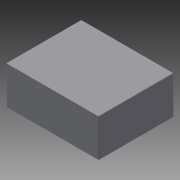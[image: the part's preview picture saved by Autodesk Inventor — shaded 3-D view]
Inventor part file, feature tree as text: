
AUTODESK INVENTOR PART (.ipt)
format: ipt  version: 2014 (Build 180170000, 170)  size: 89,088 bytes
history: native  units: in
note: dims shown in document units (in); Inventor stores cm internally (conversion verified against a paired STEP export)
features: reference x3, extrude x1, fillet x1, sketch x1
ambient origin geometry x8: Origin, YZ Plane, XZ Plane, XY Plane, X Axis, Y Axis, Z Axis, Center Point
bodies: Solid1 (feature_tree)
feature tree (6):
  extrude  "Extrusion1"  Depth=2.97in
  fillet  "Fillet1"  Radius=5.74in
  sketch  "Sketch1"  dims[d0=7.07in d1=2.97in d2=5.74in d3=0.0in d4=0.05in]
  reference  "Reference1"
  reference  "Reference2"
  reference  "Reference3"
